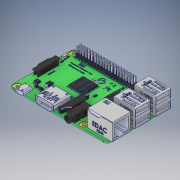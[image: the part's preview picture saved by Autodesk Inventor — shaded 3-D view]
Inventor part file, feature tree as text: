
AUTODESK INVENTOR PART (.ipt)
format: ipt  version: 2018 (Build 220112000, 112)  size: 4,628,480 bytes
history: native  units: in
note: dims shown in document units (in); Inventor stores cm internally (conversion verified against a paired STEP export)
features: other x65, fillet x2
ambient origin geometry x8: Origin, YZ Plane, XZ Plane, XY Plane, X Axis, Y Axis, Z Axis, Center Point
bodies: Solid1 (feature_tree), Solid2 (feature_tree), Solid3 (feature_tree), Solid4 (feature_tree), Solid5 (feature_tree), Solid6 (feature_tree), Solid7 (feature_tree), Solid8 (feature_tree), Solid9 (feature_tree), Solid10 (feature_tree), Solid11 (feature_tree), Solid12 (feature_tree), Solid13 (feature_tree), Solid14 (feature_tree), Solid15 (feature_tree), Solid16 (feature_tree), Solid17 (feature_tree), Solid18 (feature_tree), Solid19 (feature_tree), Solid20 (feature_tree), Solid21 (feature_tree), Solid22 (feature_tree), Solid23 (feature_tree), Solid24 (feature_tree), Solid25 (feature_tree), Solid26 (feature_tree), Solid27 (feature_tree), Solid28 (feature_tree), Solid29 (feature_tree), Solid30 (feature_tree), Solid31 (feature_tree), Solid32 (feature_tree), Solid33 (feature_tree), Solid34 (feature_tree), Solid35 (feature_tree), Solid36 (feature_tree), Solid37 (feature_tree), Solid38 (feature_tree), Solid39 (feature_tree), Solid40 (feature_tree), Solid41 (feature_tree), Solid42 (feature_tree), Solid43 (feature_tree), Solid44 (feature_tree), Solid45 (feature_tree), Solid46 (feature_tree), Solid47 (feature_tree), Solid48 (feature_tree), Solid49 (feature_tree), Solid50 (feature_tree), Solid51 (feature_tree), Solid52 (feature_tree), Solid53 (feature_tree), Solid54 (feature_tree), Solid55 (feature_tree), Solid56 (feature_tree), Solid57 (feature_tree), Solid58 (feature_tree), Solid59 (feature_tree), Solid60 (feature_tree), Solid61 (feature_tree), Solid62 (feature_tree), Solid63 (feature_tree), Solid64 (feature_tree), Solid65 (feature_tree), Solid66 (feature_tree), Solid67 (feature_tree)
feature tree (67):
  other  "Cut-Extrude49"
  other  "Cut-Extrude63"
  other  "Boss-Extrude13[1]"
  other  "Boss-Extrude13[2]"
  other  "LPattern13[1]"
  other  "LPattern13[2]"
  other  "LPattern13[3]"
  other  "LPattern13[4]"
  other  "LPattern13[5]"
  other  "LPattern13[6]"
  other  "LPattern13[7]"
  other  "LPattern13[8]"
  other  "LPattern13[9]"
  other  "LPattern13[10]"
  other  "LPattern13[11]"
  other  "LPattern13[12]"
  other  "LPattern13[13]"
  other  "LPattern13[14]"
  other  "LPattern13[15]"
  other  "LPattern13[16]"
  other  "LPattern13[17]"
  other  "LPattern13[18]"
  other  "Boss-Extrude14[1]"
  other  "Boss-Extrude14[2]"
  other  "LPattern14[1]"
  other  "LPattern14[2]"
  other  "LPattern14[3]"
  other  "LPattern14[4]"
  other  "LPattern14[5]"
  other  "LPattern14[6]"
  other  "LPattern14[7]"
  other  "LPattern14[8]"
  other  "LPattern14[9]"
  other  "LPattern14[10]"
  other  "LPattern14[11]"
  other  "LPattern14[12]"
  other  "LPattern14[13]"
  other  "LPattern14[14]"
  other  "LPattern14[15]"
  other  "LPattern14[16]"
  other  "LPattern14[17]"
  other  "LPattern14[18]"
  other  "Boss-Extrude18[1]"
  other  "Boss-Extrude18[2]"
  other  "LPattern17[1]"
  other  "LPattern17[2]"
  other  "LPattern17[3]"
  other  "LPattern17[4]"
  other  "LPattern17[5]"
  other  "LPattern17[6]"
  other  "Boss-Extrude19[1]"
  other  "Boss-Extrude19[2]"
  other  "LPattern18[1]"
  other  "LPattern18[2]"
  other  "LPattern18[3]"
  other  "LPattern18[4]"
  fillet  "Fillet20"  [1 undecoded]
  fillet  "Fillet21"  [1 undecoded]
  other  "Boss-Extrude21"
  other  "LPattern19"
  other  "Boss-Extrude23"
  other  "LPattern20"
  other  "Boss-Extrude24"
  other  "Boss-Extrude25[1]"
  other  "Boss-Extrude25[2]"
  other  "Cut-Extrude84"
  other  "Boss-Extrude26"
note: 2 required parameter values undecoded (feature->parameter linkage not recoverable at this tier; creation-order binding heuristic only, values carry confidence <= 0.55)
